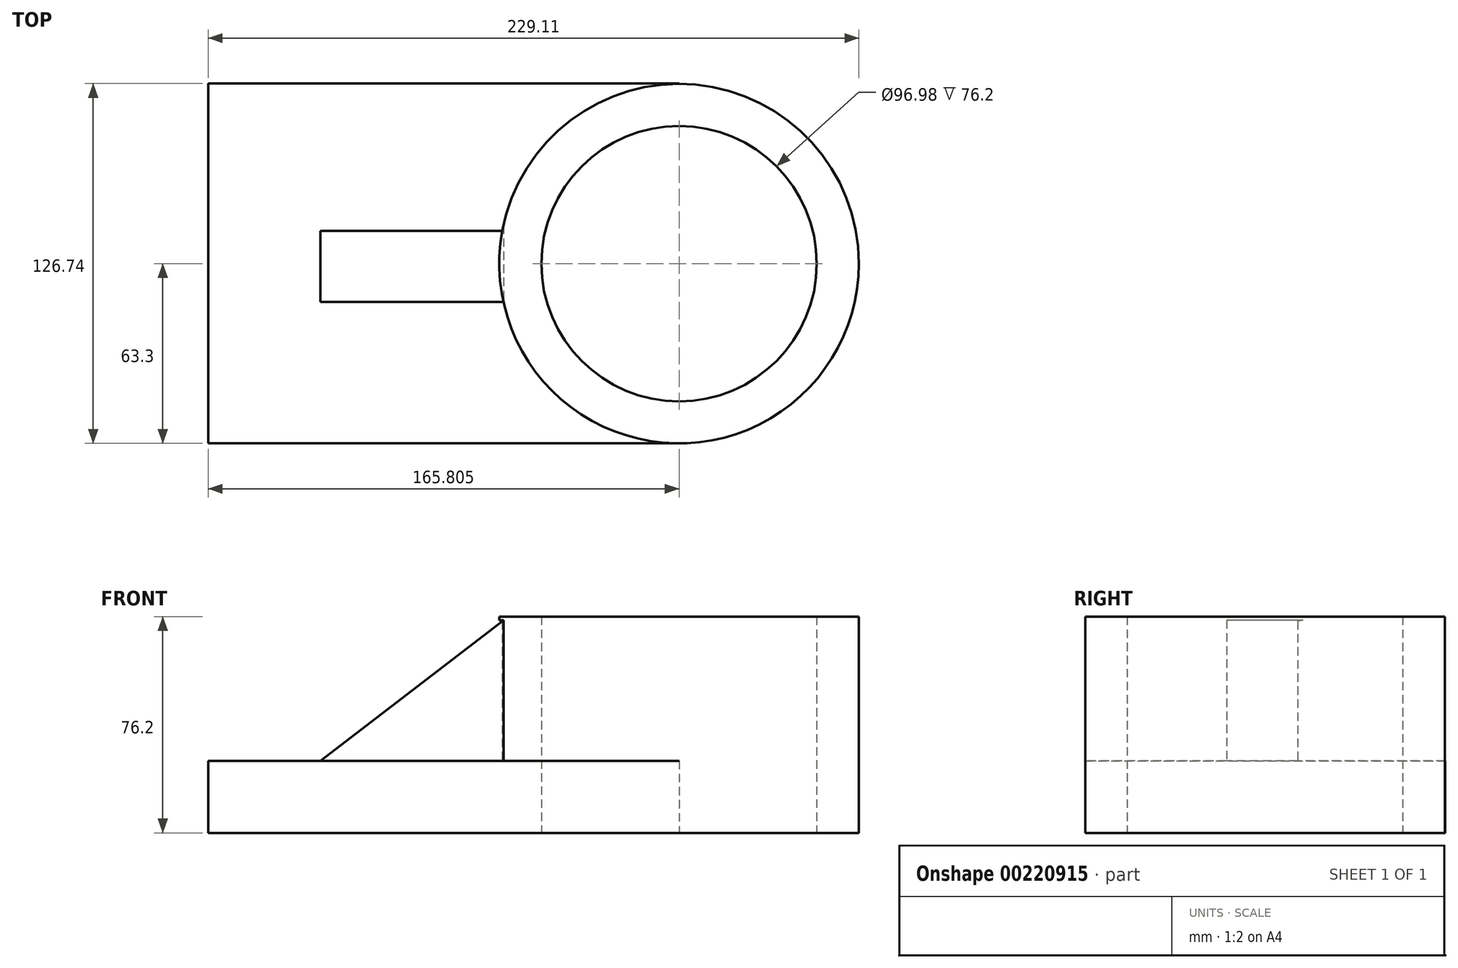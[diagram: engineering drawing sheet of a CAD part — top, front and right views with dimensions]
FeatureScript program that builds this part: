
annotation { "Feature Type Name" : "Feature", "Feature Type Description" : "" }
export const myFeature = defineFeature(function(context is Context, id is Id, definition is map)
    precondition{}
    {
        {
            var Q0;
            Q0=qCreatedBy(makeId("Top.planeOp"),FACE);
            var sketch = newSketch(context, id + "F0", { "sketchPlane" : qUnion([Q0])});
            skCircle(sketch, "E0", {"center": v(41.62, 0) * mm, "radius": 63.3 * mm});
            skCircle(sketch, "E1", {"center": v(41.62, 0) * mm, "radius": 48.49 * mm});
            skLineSegment(sketch, "E2.bottom", {"start": v(41.62, -63.3) * mm, "end": v(-124.2, -63.3) * mm});
            skLineSegment(sketch, "E2.top", {"start": v(41.62, 63.44) * mm, "end": v(-124.2, 63.44) * mm});
            skLineSegment(sketch, "E2.right", {"start": v(-124.2, -63.3) * mm, "end": v(-124.2, 63.44) * mm});
            skLineSegment(sketch, "E3.bottom", {"start": v(-20.63, 11.52) * mm, "end": v(-84.67, 11.52) * mm});
            skLineSegment(sketch, "E3.top", {"start": v(-4.96, -13.5) * mm, "end": v(-5.48, -13.5) * mm});
            skLineSegment(sketch, "E3.right", {"start": v(-84.67, 11.52) * mm, "end": v(-84.67, -13.5) * mm});
            skPoint(sketch, "E4.orphan", {"position": v(-5.48, 11.52) * mm});
            skPoint(sketch, "E5.start.orphan", {"position": v(-5.48, -13.5) * mm});
            skLineSegment(sketch, "E6.trimOffspring", {"start": v(-20.23, -13.5) * mm, "end": v(-84.67, -13.5) * mm});
            skLineSegment(sketch, "E7.trimOffspring", {"start": v(41.62, 63.3) * mm, "end": v(41.62, 63.44) * mm});
            skSolve(sketch);
        }
        {
            var Q0;
            Q0=makeQuery(id+"F0.imprint","IMPRINT",FACE,{"disambiguationData":[TD([[makeQuery(id+"F0.imprint","IMPRINT",EDGE,{"derivedFrom":sQuery(id+"F0.wireOp",EDGE,"E1")}),-1.0]])]});
            extrude(context, id + "F1", {"entities" : qUnion([Q0]), "depth" : 76.2 * mm});
        }
        {
            var Q0;
            {var subQ0=sQuery(id+"F0.wireOp",EDGE,"E2.bottom");Q0=makeQuery(id+"F0.imprint","IMPRINT",FACE,{"disambiguationData":[TD([[makeQuery(id+"F0.imprint","IMPRINT",EDGE,{"derivedFrom":subQ0}),-1.0]])]});}
            extrude(context, id + "F2", {"entities" : qUnion([Q0]), "operationType" : NewBodyOperationType.ADD, "depth" : 25.4 * mm});
        }
        {
            var Q0;
            {var subQ0=sQuery(id+"F0.wireOp",EDGE,"E3.bottom");Q0=makeQuery(id+"F0.imprint","IMPRINT",FACE,{"disambiguationData":[TD([[makeQuery(id+"F0.imprint","IMPRINT",EDGE,{"derivedFrom":subQ0}),1.0]])]});}
            extrude(context, id + "F3", {"entities" : qUnion([Q0]), "operationType" : NewBodyOperationType.ADD, "depth" : 74.93 * mm});
        }
        {
            var Q0;
            Q0=makeQuery(id+"F3.opExtrude","SWEPT_FACE",FACE,{"disambiguationData":[OSD([sQuery(id+"F0.wireOp",EDGE,"E6.trimOffspring")])]});
            var sketch = newSketch(context, id + "F4", { "sketchPlane" : qUnion([Q0])});
            skLineSegment(sketch, "E8.0", {"start": v(-20.23, 74.93) * mm, "end": v(-84.67, 74.93) * mm});
            skLineSegment(sketch, "E9.0", {"start": v(-84.67, 74.93) * mm, "end": v(-84.67, 25.4) * mm});
            skLineSegment(sketch, "E10", {"start": v(-20.23, 74.93) * mm, "end": v(-84.67, 25.4) * mm});
            skSolve(sketch);
        }
        {
            var Q0;
            Q0=makeQuery(id+"F4.imprint","IMPRINT",FACE,{"disambiguationData":[TD([[makeQuery(id+"F4.imprint","IMPRINT",EDGE,{"derivedFrom":sQuery(id+"F4.wireOp",EDGE,"E8.0")}),1.0]])]});
            extrude(context, id + "F5", {"entities" : qUnion([Q0]), "operationType" : NewBodyOperationType.REMOVE, "endBound" : BoundingType.THROUGH_ALL, "oppositeDirection" : true, "depth" : 25.4 * mm});
        }
    });
